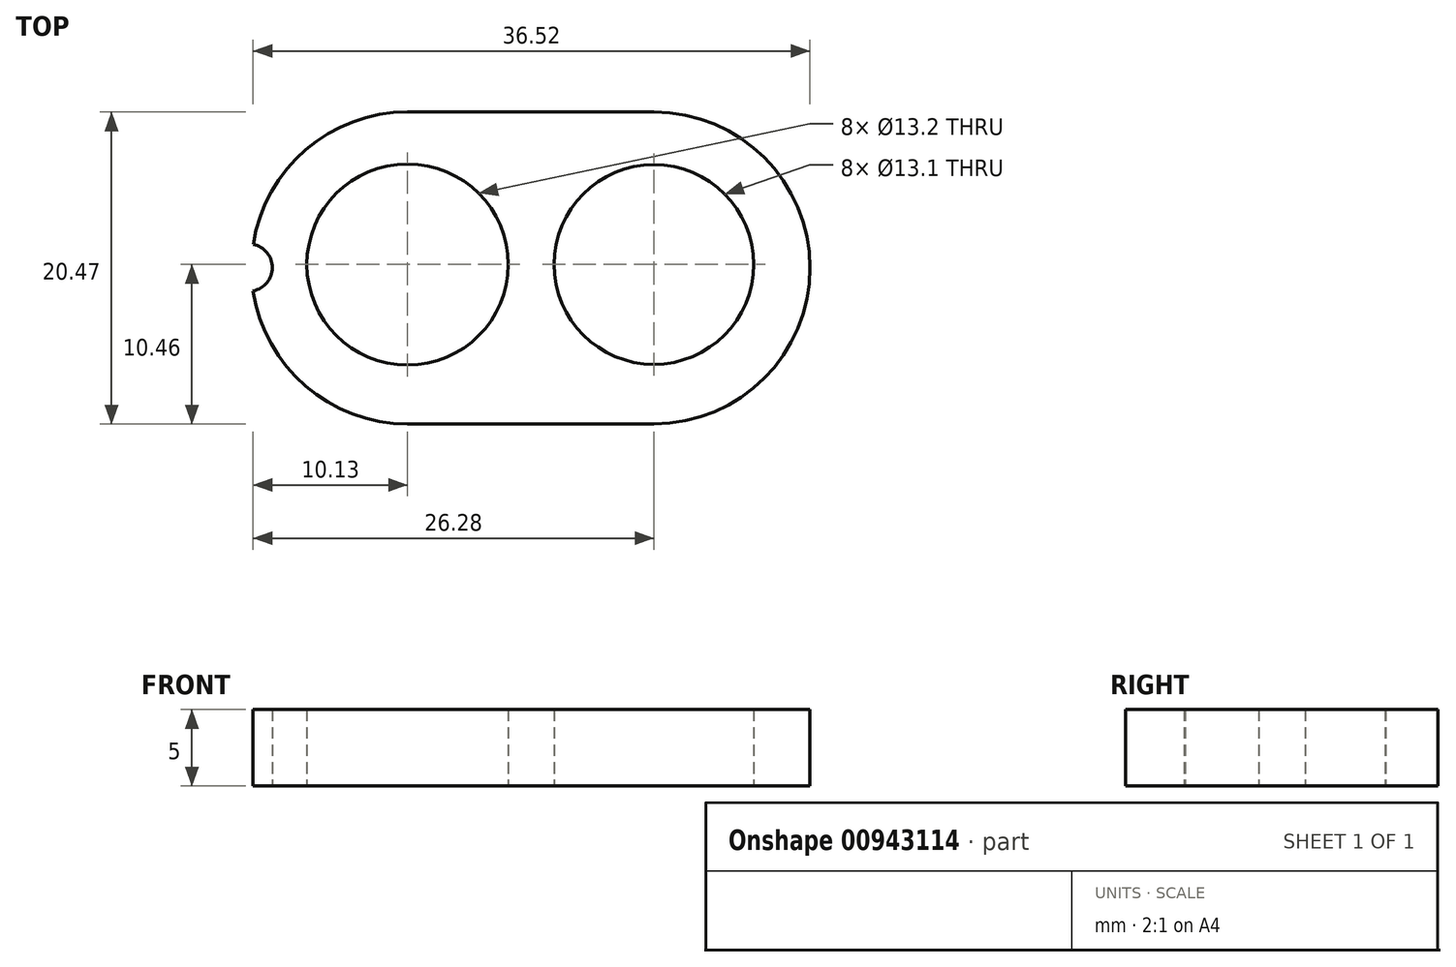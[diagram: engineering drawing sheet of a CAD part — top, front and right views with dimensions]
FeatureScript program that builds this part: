
annotation { "Feature Type Name" : "Feature", "Feature Type Description" : "" }
export const myFeature = defineFeature(function(context is Context, id is Id, definition is map)
    precondition{}
    {
        {
            var Q0;
            Q0=qCreatedBy(makeId("Top.planeOp"),FACE);
            var sketch = newSketch(context, id + "F0", { "sketchPlane" : qUnion([Q0])});
            skCircle(sketch, "E0", {"center": v(0, 0) * mm, "radius": 6.6 * mm});
            skCircle(sketch, "E1", {"center": v(16.15, 0) * mm, "radius": 6.55 * mm});
            skLineSegment(sketch, "E2", {"start": v(0, 10.01) * mm, "end": v(16.15, 10.01) * mm});
            skLineSegment(sketch, "E3", {"start": v(0, -10.46) * mm, "end": v(16.15, -10.46) * mm});
            skArc(sketch, "E4", {"start": v(0, 10.01) * mm, "mid": v(-6.67, 7.54) * mm, "end": v(-10.12, 1.31) * mm});
            skArc(sketch, "E5", {"start": v(16.15, -10.46) * mm, "mid": v(26.39, -0.22) * mm, "end": v(16.15, 10.01) * mm});
            skArc(sketch, "E6", {"start": v(-10.13, -1.72) * mm, "mid": v(-8.87, -0.2) * mm, "end": v(-10.12, 1.31) * mm});
            skArc(sketch, "E7.trimOffspring", {"start": v(-10.13, -1.72) * mm, "mid": v(-6.69, -7.97) * mm, "end": v(0, -10.46) * mm});
            skSolve(sketch);
        }
        {
            var Q0;
            Q0=qSketchRegion(id+"F0",true);
            extrude(context, id + "F1", {"entities" : qUnion([Q0]), "depth" : 5 * mm, "offsetDistance" : 25 * mm});
        }
    });
